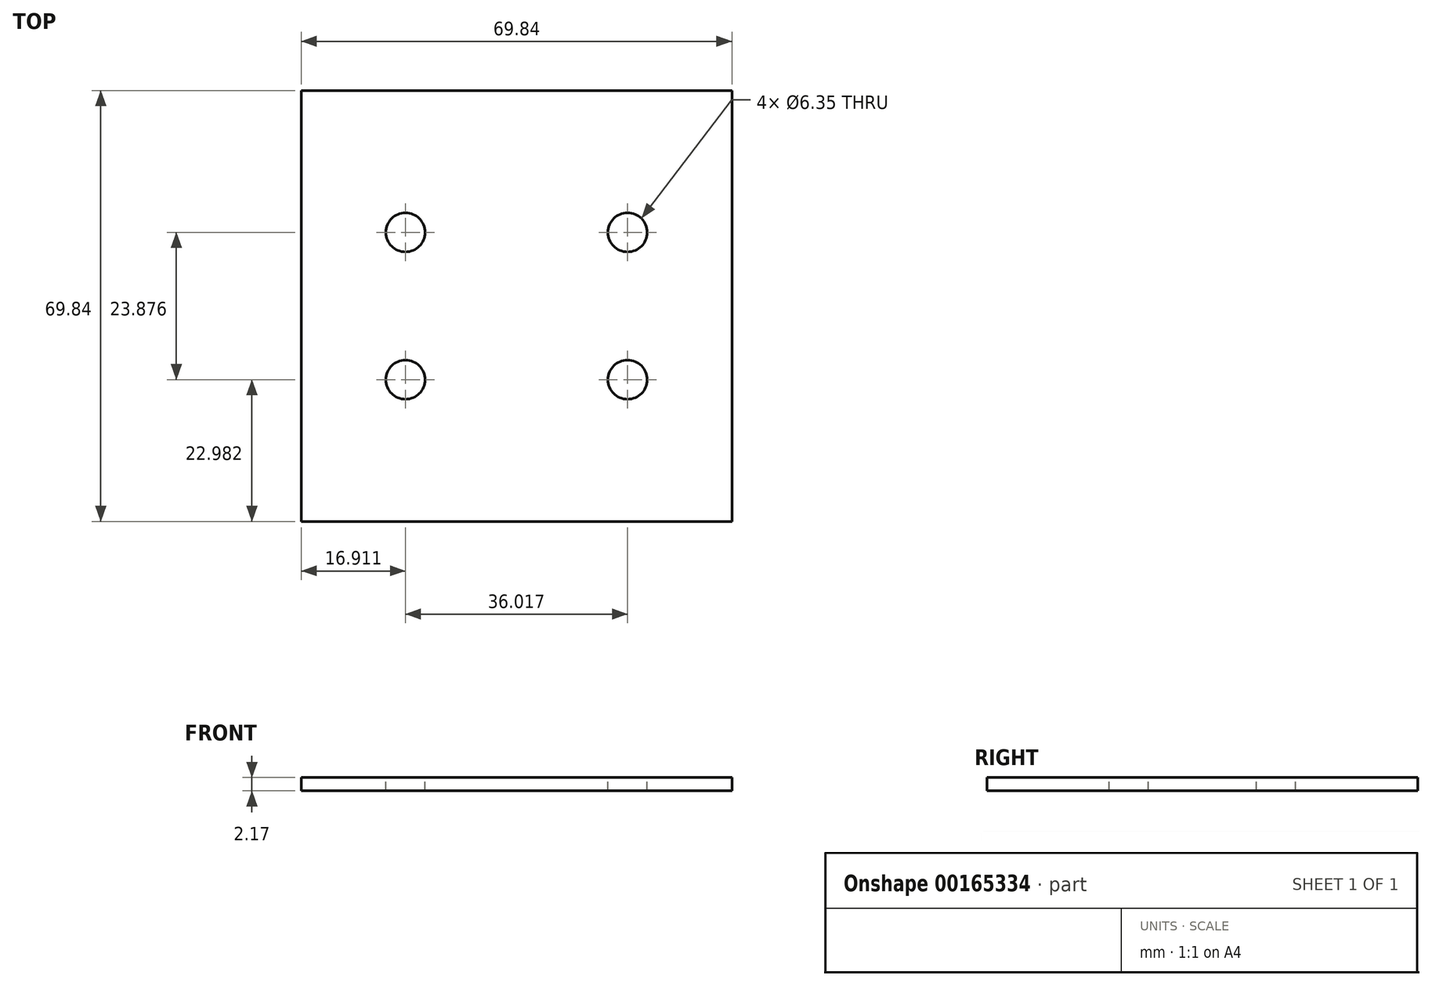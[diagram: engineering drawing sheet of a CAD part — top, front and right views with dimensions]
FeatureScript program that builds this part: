
annotation { "Feature Type Name" : "Feature", "Feature Type Description" : "" }
export const myFeature = defineFeature(function(context is Context, id is Id, definition is map)
    precondition{}
    {
        {
            var Q0;
            Q0=qCreatedBy(makeId("Top.planeOp"),FACE);
            var sketch = newSketch(context, id + "F0", { "sketchPlane" : qUnion([Q0])});
            skLineSegment(sketch, "E0.bottom", {"start": v(34.93, -34.92) * mm, "end": v(-34.93, -34.93) * mm});
            skLineSegment(sketch, "E0.top", {"start": v(34.93, 34.93) * mm, "end": v(-34.93, 34.92) * mm});
            skLineSegment(sketch, "E0.left", {"start": v(34.93, -34.92) * mm, "end": v(34.93, 34.93) * mm});
            skLineSegment(sketch, "E0.right", {"start": v(-34.93, -34.93) * mm, "end": v(-34.93, 34.92) * mm});
            skPoint(sketch, "E0.middle", {"position": v(0, 0) * mm});
            skSolve(sketch);
        }
        {
            var Q0;
            Q0=qSketchRegion(id+"F0",true);
            extrude(context, id + "F1", {"entities" : qUnion([Q0]), "depth" : 2.17 * mm});
        }
        {
            var Q0;
            Q0=makeQuery(id+"F1.opExtrude","CAP_FACE",FACE,{"disambiguationData":[OSD([sQuery(id+"F0.wireOp",EDGE,"E0.bottom"),sQuery(id+"F0.wireOp",EDGE,"E0.top"),sQuery(id+"F0.wireOp",EDGE,"E0.left"),sQuery(id+"F0.wireOp",EDGE,"E0.right")])],"isStart":false});
            var sketch = newSketch(context, id + "F2", { "sketchPlane" : qUnion([Q0])});
            skLineSegment(sketch, "E1", {"start": v(0, 0) * mm, "end": v(-18, 0) * mm, "construction": true});
            skLineSegment(sketch, "E2", {"start": v(0, 0) * mm, "end": v(18, 0) * mm, "construction": true});
            skLineSegment(sketch, "E3", {"start": v(0, 0) * mm, "end": v(0, 11.94) * mm, "construction": true});
            skLineSegment(sketch, "E4", {"start": v(0, 0) * mm, "end": v(0, -11.94) * mm, "construction": true});
            skLineSegment(sketch, "E5.bottom", {"start": v(18, -11.94) * mm, "end": v(-18, -11.94) * mm, "construction": true});
            skLineSegment(sketch, "E5.top", {"start": v(18, 11.94) * mm, "end": v(-18, 11.94) * mm, "construction": true});
            skLineSegment(sketch, "E5.left", {"start": v(18, -11.94) * mm, "end": v(18, 11.94) * mm, "construction": true});
            skLineSegment(sketch, "E5.right", {"start": v(-18, -11.94) * mm, "end": v(-18, 11.94) * mm, "construction": true});
            skPoint(sketch, "E5.middle", {"position": v(0, 0) * mm});
            skCircle(sketch, "E6", {"center": v(-18, 11.94) * mm, "radius": 3.18 * mm});
            skCircle(sketch, "E7", {"center": v(-18, -11.94) * mm, "radius": 3.18 * mm});
            skCircle(sketch, "E8", {"center": v(18, -11.94) * mm, "radius": 3.18 * mm});
            skCircle(sketch, "E9", {"center": v(18, 11.94) * mm, "radius": 3.18 * mm});
            skSolve(sketch);
        }
        {
            var Q0;
            Q0=qSketchRegion(id+"F2",true);
            extrude(context, id + "F3", {"entities" : qUnion([Q0]), "operationType" : NewBodyOperationType.REMOVE, "endBound" : BoundingType.THROUGH_ALL, "oppositeDirection" : true, "depth" : 25.4 * mm});
        }
    });
